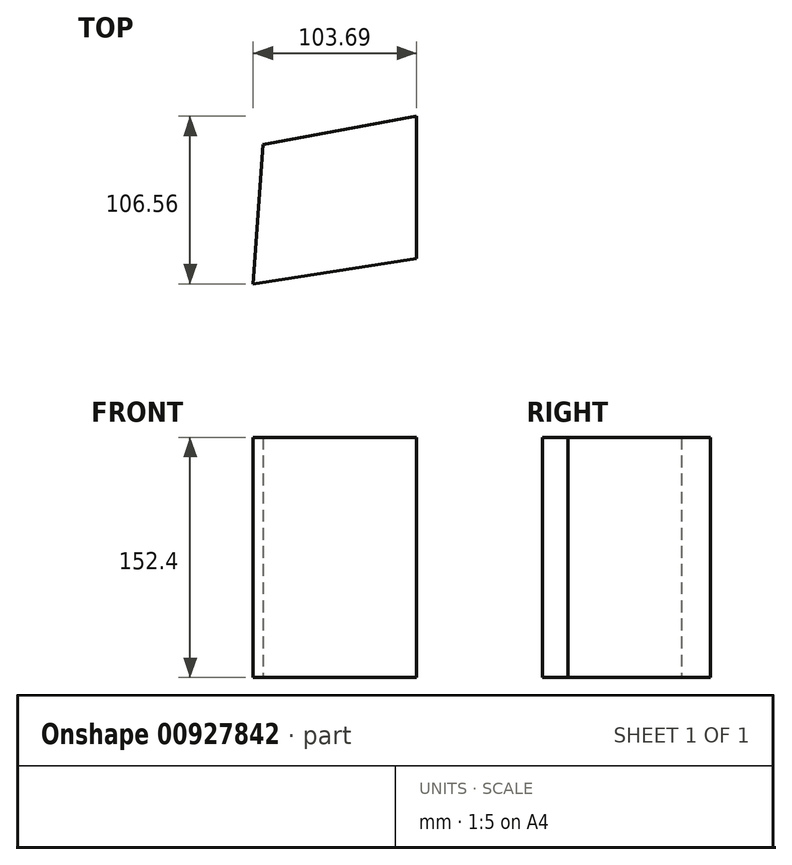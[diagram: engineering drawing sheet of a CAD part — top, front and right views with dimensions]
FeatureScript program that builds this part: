
annotation { "Feature Type Name" : "Feature", "Feature Type Description" : "" }
export const myFeature = defineFeature(function(context is Context, id is Id, definition is map)
    precondition{}
    {
        {
            var Q0;
            Q0=qCreatedBy(makeId("Top.planeOp"),FACE);
            var sketch = newSketch(context, id + "F0", { "sketchPlane" : qUnion([Q0])});
            skLineSegment(sketch, "E0", {"start": v(-54.74, -45.37) * mm, "end": v(48.95, -29.2) * mm});
            skLineSegment(sketch, "E1", {"start": v(48.95, -29.2) * mm, "end": v(48.95, 61.2) * mm});
            skLineSegment(sketch, "E2", {"start": v(48.95, 61.2) * mm, "end": v(-48.48, 43.02) * mm});
            skLineSegment(sketch, "E3", {"start": v(-48.48, 43.02) * mm, "end": v(-54.74, -45.37) * mm});
            skSolve(sketch);
        }
        {
            var Q0;
            Q0=makeQuery(id+"F0.imprint","IMPRINT",FACE,{"disambiguationData":[TD([[makeQuery(id+"F0.imprint","IMPRINT",EDGE,{"derivedFrom":sQuery(id+"F0.wireOp",EDGE,"E0")}),1.0]])]});
            extrude(context, id + "F1", {"entities" : qUnion([Q0]), "depth" : 152.4 * mm, "offsetDistance" : 25.4 * mm});
        }
    });
